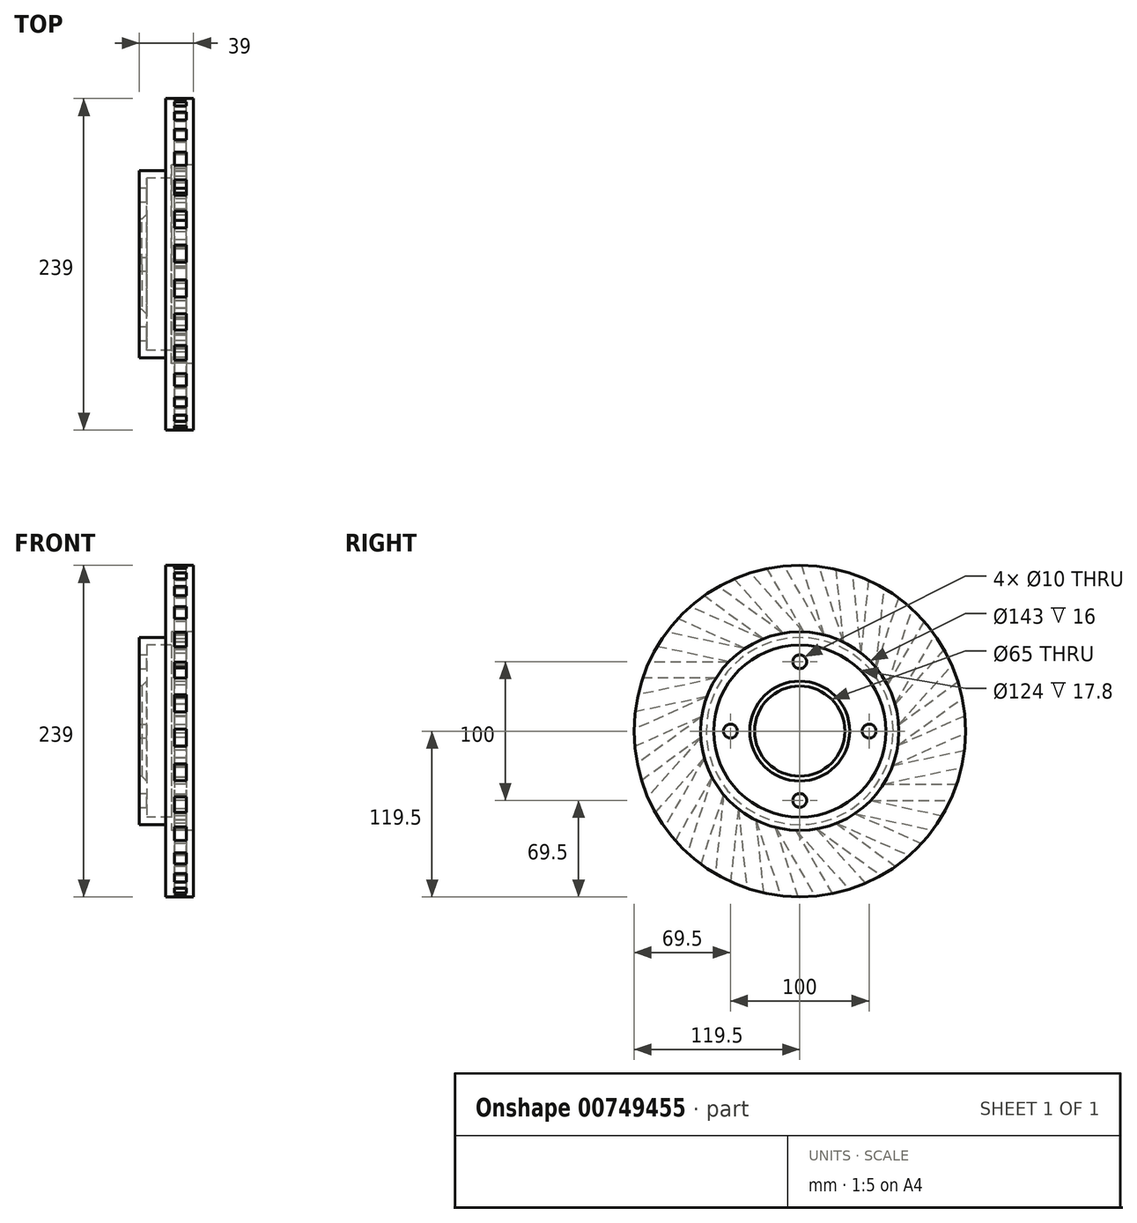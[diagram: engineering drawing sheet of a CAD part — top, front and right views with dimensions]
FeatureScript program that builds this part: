
annotation { "Feature Type Name" : "Feature", "Feature Type Description" : "" }
export const myFeature = defineFeature(function(context is Context, id is Id, definition is map)
    precondition{}
    {
        {
            var Q0;
            Q0=qCreatedBy(makeId("Front.planeOp"),FACE);
            var sketch = newSketch(context, id + "F0", { "sketchPlane" : qUnion([Q0])});
            skLineSegment(sketch, "E0", {"start": v(0, 32.5) * mm, "end": v(0, 67.4) * mm});
            skLineSegment(sketch, "E1", {"start": v(0, 67.4) * mm, "end": v(19, 67.4) * mm});
            skLineSegment(sketch, "E2", {"start": v(19, 67.4) * mm, "end": v(19, 119.5) * mm});
            skLineSegment(sketch, "E3", {"start": v(19, 119.5) * mm, "end": v(39, 119.5) * mm});
            skLineSegment(sketch, "E4", {"start": v(39, 119.5) * mm, "end": v(39, 71.5) * mm});
            skLineSegment(sketch, "E5", {"start": v(39, 71.5) * mm, "end": v(23, 71.5) * mm});
            skLineSegment(sketch, "E6", {"start": v(23, 71.5) * mm, "end": v(23, 62) * mm});
            skLineSegment(sketch, "E7", {"start": v(23, 62) * mm, "end": v(5.2, 62) * mm});
            skLineSegment(sketch, "E8", {"start": v(5.2, 62) * mm, "end": v(5.2, 32.5) * mm});
            skLineSegment(sketch, "E9", {"start": v(5.2, 32.5) * mm, "end": v(0, 32.5) * mm});
            skLineSegment(sketch, "E10", {"start": v(2.46, 0) * mm, "end": v(32.27, 0) * mm, "construction": true});
            skSolve(sketch);
        }
        {
            var Q0;
            Q0=makeQuery(id+"F0.imprint","IMPRINT",FACE,{"disambiguationData":[TD([[makeQuery(id+"F0.imprint","IMPRINT",EDGE,{"derivedFrom":sQuery(id+"F0.wireOp",EDGE,"E0")}),-1.0]])]});
            var Q1;
            Q1=sQuery(id+"F0.wireOp",EDGE,"E5");
            var Q2;
            Q2=sQuery(id+"F0.wireOp",EDGE,"E4");
            var Q3;
            Q3=sQuery(id+"F0.wireOp",EDGE,"E8");
            var Q4;
            Q4=sQuery(id+"F0.wireOp",EDGE,"E3");
            var Q5;
            Q5=sQuery(id+"F0.wireOp",EDGE,"E7");
            var Q6;
            Q6=sQuery(id+"F0.wireOp",EDGE,"E2");
            var Q7;
            Q7=sQuery(id+"F0.wireOp",EDGE,"E1");
            var Q8;
            Q8=sQuery(id+"F0.wireOp",EDGE,"E0");
            var Q9;
            Q9=sQuery(id+"F0.wireOp",EDGE,"E9");
            var Q10;
            Q10=sQuery(id+"F0.wireOp",EDGE,"E6");
            var Q11;
            Q11=sQuery(id+"F0.wireOp",EDGE,"E10");
            revolve(context, id + "F1", {"surfaceOperationType" : NewSurfaceOperationType.NEW, "entities" : qUnion([Q0]), "surfaceEntities" : qUnion([Q1, Q2, Q3, Q4, Q5, Q6, Q7, Q8, Q9, Q10]), "axis" : qUnion([Q11]), "revolveType" : RevolveType.FULL});
        }
        {
            var Q0;
            Q0=makeQuery(id+"F1.opRevolve","SWEPT_EDGE",EDGE,{"disambiguationData":[OSD([sQuery(id+"F0.wireOp",VERTEX,"E9.start")])]});
            var Q1;
            Q1=makeQuery(id+"F1.opRevolve","SWEPT_EDGE",EDGE,{"disambiguationData":[OSD([sQuery(id+"F0.wireOp",EDGE,"E8"),sQuery(id+"F0.wireOp",EDGE,"E9")])]});
            chamfer(context, id + "F2", {"entities" : qUnion([Q0, Q1]), "width" : 3.5 * mm, "tangentPropagation" : true});
        }
        {
            var Q0;
            Q0=makeQuery(id+"F1.opRevolve","SWEPT_FACE",FACE,{"disambiguationData":[OSD([sQuery(id+"F0.wireOp",EDGE,"E2")])]});
            var sketch = newSketch(context, id + "F3", { "sketchPlane" : qUnion([Q0])});
            skCircle(sketch, "E11", {"center": v(0, 50) * mm, "radius": 5 * mm});
            skCircle(sketch, "E12.1.0", {"center": v(-50, 0) * mm, "radius": 5 * mm});
            skCircle(sketch, "E12.2.0", {"center": v(0, -50) * mm, "radius": 5 * mm});
            skCircle(sketch, "E12.3.0", {"center": v(50, 0) * mm, "radius": 5 * mm});
            skPoint(sketch, "E12.center", {"position": v(0, 0) * mm});
            skSolve(sketch);
        }
        {
            var Q0;
            Q0=makeQuery(id+"F3.imprint","IMPRINT",FACE,{"disambiguationData":[TD([[makeQuery(id+"F3.imprint","IMPRINT",EDGE,{"derivedFrom":sQuery(id+"F3.wireOp",EDGE,"E11")}),1.0]])]});
            var Q1;
            Q1=makeQuery(id+"F3.imprint","IMPRINT",FACE,{"disambiguationData":[TD([[makeQuery(id+"F3.imprint","IMPRINT",EDGE,{"derivedFrom":sQuery(id+"F3.wireOp",EDGE,"E12.1.0")}),1.0]])]});
            var Q2;
            Q2=makeQuery(id+"F3.imprint","IMPRINT",FACE,{"disambiguationData":[TD([[makeQuery(id+"F3.imprint","IMPRINT",EDGE,{"derivedFrom":sQuery(id+"F3.wireOp",EDGE,"E12.3.0")}),1.0]])]});
            var Q3;
            Q3=makeQuery(id+"F3.imprint","IMPRINT",FACE,{"disambiguationData":[TD([[makeQuery(id+"F3.imprint","IMPRINT",EDGE,{"derivedFrom":sQuery(id+"F3.wireOp",EDGE,"E12.2.0")}),1.0]])]});
            extrude(context, id + "F4", {"entities" : qUnion([Q0, Q1, Q2, Q3]), "operationType" : NewBodyOperationType.REMOVE, "endBound" : BoundingType.THROUGH_ALL, "depth" : 25 * mm, "offsetDistance" : 25 * mm});
        }
        {
            var Q0;
            Q0=makeQuery(id+"F1.opRevolve","SWEPT_FACE",FACE,{"disambiguationData":[OSD([sQuery(id+"F0.wireOp",EDGE,"E4")])]});
            var sketch = newSketch(context, id + "F5", { "sketchPlane" : qUnion([Q0])});
            skLineSegment(sketch, "E13.bottom", {"start": v(-37.23, 38.26) * mm, "end": v(-217.01, 38.26) * mm});
            skLineSegment(sketch, "E13.top", {"start": v(-37.23, 49.86) * mm, "end": v(-217.01, 49.86) * mm});
            skLineSegment(sketch, "E13.left", {"start": v(-37.23, 38.26) * mm, "end": v(-37.23, 49.86) * mm});
            skLineSegment(sketch, "E13.right", {"start": v(-217.01, 38.26) * mm, "end": v(-217.01, 49.86) * mm});
            skPoint(sketch, "E13.middle", {"position": v(-127.12, 44.06) * mm});
            skLineSegment(sketch, "E14.1.0", {"start": v(-46.78, 41.03) * mm, "end": v(-222.63, 3.65) * mm});
            skLineSegment(sketch, "E14.1.1", {"start": v(-44.37, 29.68) * mm, "end": v(-46.78, 41.03) * mm});
            skLineSegment(sketch, "E14.1.2", {"start": v(-44.37, 29.68) * mm, "end": v(-220.22, -7.7) * mm});
            skLineSegment(sketch, "E14.1.3", {"start": v(-220.22, -7.7) * mm, "end": v(-222.63, 3.65) * mm});
            skLineSegment(sketch, "E14.2.0", {"start": v(-54.29, 30.4) * mm, "end": v(-218.53, -42.72) * mm});
            skLineSegment(sketch, "E14.2.1", {"start": v(-49.57, 19.81) * mm, "end": v(-54.29, 30.4) * mm});
            skLineSegment(sketch, "E14.2.2", {"start": v(-49.57, 19.81) * mm, "end": v(-213.81, -53.31) * mm});
            skLineSegment(sketch, "E14.2.3", {"start": v(-213.81, -53.31) * mm, "end": v(-218.53, -42.72) * mm});
            skLineSegment(sketch, "E14.3.0", {"start": v(-59.42, 18.46) * mm, "end": v(-204.87, -87.22) * mm});
            skLineSegment(sketch, "E14.3.1", {"start": v(-52.6, 9.07) * mm, "end": v(-59.42, 18.46) * mm});
            skLineSegment(sketch, "E14.3.2", {"start": v(-52.6, 9.07) * mm, "end": v(-198.05, -96.6) * mm});
            skLineSegment(sketch, "E14.3.3", {"start": v(-198.05, -96.6) * mm, "end": v(-204.87, -87.22) * mm});
            skLineSegment(sketch, "E14.4.0", {"start": v(-61.96, 5.7) * mm, "end": v(-182.26, -127.9) * mm});
            skLineSegment(sketch, "E14.4.1", {"start": v(-53.34, -2.06) * mm, "end": v(-61.96, 5.7) * mm});
            skLineSegment(sketch, "E14.4.2", {"start": v(-53.34, -2.06) * mm, "end": v(-173.64, -135.67) * mm});
            skLineSegment(sketch, "E14.4.3", {"start": v(-173.64, -135.67) * mm, "end": v(-182.26, -127.9) * mm});
            skLineSegment(sketch, "E14.5.0", {"start": v(-61.8, -7.3) * mm, "end": v(-151.68, -163) * mm});
            skLineSegment(sketch, "E14.5.1", {"start": v(-51.75, -13.1) * mm, "end": v(-61.8, -7.3) * mm});
            skLineSegment(sketch, "E14.5.2", {"start": v(-51.75, -13.1) * mm, "end": v(-141.64, -168.8) * mm});
            skLineSegment(sketch, "E14.5.3", {"start": v(-141.64, -168.8) * mm, "end": v(-151.68, -163) * mm});
            skLineSegment(sketch, "E14.6.0", {"start": v(-58.92, -20) * mm, "end": v(-114.48, -190.98) * mm});
            skLineSegment(sketch, "E14.6.1", {"start": v(-47.89, -23.58) * mm, "end": v(-58.92, -20) * mm});
            skLineSegment(sketch, "E14.6.2", {"start": v(-47.89, -23.58) * mm, "end": v(-103.45, -194.57) * mm});
            skLineSegment(sketch, "E14.6.3", {"start": v(-103.45, -194.57) * mm, "end": v(-114.48, -190.98) * mm});
            skLineSegment(sketch, "E14.7.0", {"start": v(-53.48, -31.8) * mm, "end": v(-72.27, -210.6) * mm});
            skLineSegment(sketch, "E14.7.1", {"start": v(-41.94, -33.02) * mm, "end": v(-53.48, -31.8) * mm});
            skLineSegment(sketch, "E14.7.2", {"start": v(-41.94, -33.02) * mm, "end": v(-60.73, -211.82) * mm});
            skLineSegment(sketch, "E14.7.3", {"start": v(-60.73, -211.82) * mm, "end": v(-72.27, -210.6) * mm});
            skLineSegment(sketch, "E14.8.0", {"start": v(-45.7, -42.23) * mm, "end": v(-26.9, -221.03) * mm});
            skLineSegment(sketch, "E14.8.1", {"start": v(-34.16, -41.02) * mm, "end": v(-45.7, -42.23) * mm});
            skLineSegment(sketch, "E14.8.2", {"start": v(-34.16, -41.02) * mm, "end": v(-15.37, -219.82) * mm});
            skLineSegment(sketch, "E14.8.3", {"start": v(-15.37, -219.82) * mm, "end": v(-26.9, -221.03) * mm});
            skLineSegment(sketch, "E14.9.0", {"start": v(-35.91, -50.81) * mm, "end": v(19.64, -221.8) * mm});
            skLineSegment(sketch, "E14.9.1", {"start": v(-24.88, -47.23) * mm, "end": v(-35.91, -50.81) * mm});
            skLineSegment(sketch, "E14.9.2", {"start": v(-24.88, -47.23) * mm, "end": v(30.67, -218.21) * mm});
            skLineSegment(sketch, "E14.9.3", {"start": v(30.67, -218.21) * mm, "end": v(19.64, -221.8) * mm});
            skLineSegment(sketch, "E14.10.0", {"start": v(-24.57, -57.17) * mm, "end": v(65.33, -212.87) * mm});
            skLineSegment(sketch, "E14.10.1", {"start": v(-14.52, -51.37) * mm, "end": v(-24.57, -57.17) * mm});
            skLineSegment(sketch, "E14.10.2", {"start": v(-14.52, -51.37) * mm, "end": v(75.37, -207.07) * mm});
            skLineSegment(sketch, "E14.10.3", {"start": v(75.37, -207.07) * mm, "end": v(65.33, -212.87) * mm});
            skLineSegment(sketch, "E14.11.0", {"start": v(-12.14, -61.03) * mm, "end": v(108.16, -194.63) * mm});
            skLineSegment(sketch, "E14.11.1", {"start": v(-3.52, -53.26) * mm, "end": v(-12.14, -61.03) * mm});
            skLineSegment(sketch, "E14.11.2", {"start": v(-3.52, -53.26) * mm, "end": v(116.78, -186.87) * mm});
            skLineSegment(sketch, "E14.11.3", {"start": v(116.78, -186.87) * mm, "end": v(108.16, -194.63) * mm});
            skLineSegment(sketch, "E14.12.0", {"start": v(0.8, -62.22) * mm, "end": v(146.26, -167.9) * mm});
            skLineSegment(sketch, "E14.12.1", {"start": v(7.63, -52.83) * mm, "end": v(0.8, -62.22) * mm});
            skLineSegment(sketch, "E14.12.2", {"start": v(7.63, -52.83) * mm, "end": v(153.08, -158.5) * mm});
            skLineSegment(sketch, "E14.12.3", {"start": v(153.08, -158.5) * mm, "end": v(146.26, -167.9) * mm});
            skLineSegment(sketch, "E14.13.0", {"start": v(13.73, -60.69) * mm, "end": v(177.97, -133.81) * mm});
            skLineSegment(sketch, "E14.13.1", {"start": v(18.45, -50.1) * mm, "end": v(13.73, -60.69) * mm});
            skLineSegment(sketch, "E14.13.2", {"start": v(18.45, -50.1) * mm, "end": v(182.69, -123.22) * mm});
            skLineSegment(sketch, "E14.13.3", {"start": v(182.69, -123.22) * mm, "end": v(177.97, -133.81) * mm});
            skLineSegment(sketch, "E14.14.0", {"start": v(26.05, -56.5) * mm, "end": v(201.9, -93.89) * mm});
            skLineSegment(sketch, "E14.14.1", {"start": v(28.46, -45.16) * mm, "end": v(26.05, -56.5) * mm});
            skLineSegment(sketch, "E14.14.2", {"start": v(28.46, -45.16) * mm, "end": v(204.31, -82.54) * mm});
            skLineSegment(sketch, "E14.14.3", {"start": v(204.31, -82.54) * mm, "end": v(201.9, -93.89) * mm});
            skLineSegment(sketch, "E14.15.0", {"start": v(37.23, -49.86) * mm, "end": v(217.01, -49.86) * mm});
            skLineSegment(sketch, "E14.15.1", {"start": v(37.23, -38.26) * mm, "end": v(37.23, -49.86) * mm});
            skLineSegment(sketch, "E14.15.2", {"start": v(37.23, -38.26) * mm, "end": v(217.01, -38.26) * mm});
            skLineSegment(sketch, "E14.15.3", {"start": v(217.01, -38.26) * mm, "end": v(217.01, -49.86) * mm});
            skLineSegment(sketch, "E14.16.0", {"start": v(46.78, -41.03) * mm, "end": v(222.63, -3.65) * mm});
            skLineSegment(sketch, "E14.16.1", {"start": v(44.37, -29.68) * mm, "end": v(46.78, -41.03) * mm});
            skLineSegment(sketch, "E14.16.2", {"start": v(44.37, -29.68) * mm, "end": v(220.22, 7.7) * mm});
            skLineSegment(sketch, "E14.16.3", {"start": v(220.22, 7.7) * mm, "end": v(222.63, -3.65) * mm});
            skLineSegment(sketch, "E14.17.0", {"start": v(54.29, -30.4) * mm, "end": v(218.53, 42.72) * mm});
            skLineSegment(sketch, "E14.17.1", {"start": v(49.57, -19.81) * mm, "end": v(54.29, -30.4) * mm});
            skLineSegment(sketch, "E14.17.2", {"start": v(49.57, -19.81) * mm, "end": v(213.81, 53.31) * mm});
            skLineSegment(sketch, "E14.17.3", {"start": v(213.81, 53.31) * mm, "end": v(218.53, 42.72) * mm});
            skLineSegment(sketch, "E14.18.0", {"start": v(59.42, -18.46) * mm, "end": v(204.87, 87.22) * mm});
            skLineSegment(sketch, "E14.18.1", {"start": v(52.6, -9.07) * mm, "end": v(59.42, -18.46) * mm});
            skLineSegment(sketch, "E14.18.2", {"start": v(52.6, -9.07) * mm, "end": v(198.05, 96.6) * mm});
            skLineSegment(sketch, "E14.18.3", {"start": v(198.05, 96.6) * mm, "end": v(204.87, 87.22) * mm});
            skLineSegment(sketch, "E14.19.0", {"start": v(61.96, -5.7) * mm, "end": v(182.26, 127.9) * mm});
            skLineSegment(sketch, "E14.19.1", {"start": v(53.34, 2.06) * mm, "end": v(61.96, -5.7) * mm});
            skLineSegment(sketch, "E14.19.2", {"start": v(53.34, 2.06) * mm, "end": v(173.64, 135.67) * mm});
            skLineSegment(sketch, "E14.19.3", {"start": v(173.64, 135.67) * mm, "end": v(182.26, 127.9) * mm});
            skLineSegment(sketch, "E14.20.0", {"start": v(61.8, 7.3) * mm, "end": v(151.68, 163) * mm});
            skLineSegment(sketch, "E14.20.1", {"start": v(51.75, 13.1) * mm, "end": v(61.8, 7.3) * mm});
            skLineSegment(sketch, "E14.20.2", {"start": v(51.75, 13.1) * mm, "end": v(141.64, 168.8) * mm});
            skLineSegment(sketch, "E14.20.3", {"start": v(141.64, 168.8) * mm, "end": v(151.68, 163) * mm});
            skLineSegment(sketch, "E14.21.0", {"start": v(58.92, 20) * mm, "end": v(114.48, 190.98) * mm});
            skLineSegment(sketch, "E14.21.1", {"start": v(47.89, 23.58) * mm, "end": v(58.92, 20) * mm});
            skLineSegment(sketch, "E14.21.2", {"start": v(47.89, 23.58) * mm, "end": v(103.45, 194.57) * mm});
            skLineSegment(sketch, "E14.21.3", {"start": v(103.45, 194.57) * mm, "end": v(114.48, 190.98) * mm});
            skLineSegment(sketch, "E14.22.0", {"start": v(53.48, 31.8) * mm, "end": v(72.27, 210.6) * mm});
            skLineSegment(sketch, "E14.22.1", {"start": v(41.94, 33.02) * mm, "end": v(53.48, 31.8) * mm});
            skLineSegment(sketch, "E14.22.2", {"start": v(41.94, 33.02) * mm, "end": v(60.73, 211.82) * mm});
            skLineSegment(sketch, "E14.22.3", {"start": v(60.73, 211.82) * mm, "end": v(72.27, 210.6) * mm});
            skLineSegment(sketch, "E14.23.0", {"start": v(45.7, 42.23) * mm, "end": v(26.9, 221.03) * mm});
            skLineSegment(sketch, "E14.23.1", {"start": v(34.16, 41.02) * mm, "end": v(45.7, 42.23) * mm});
            skLineSegment(sketch, "E14.23.2", {"start": v(34.16, 41.02) * mm, "end": v(15.37, 219.82) * mm});
            skLineSegment(sketch, "E14.23.3", {"start": v(15.37, 219.82) * mm, "end": v(26.9, 221.03) * mm});
            skLineSegment(sketch, "E14.24.0", {"start": v(35.91, 50.81) * mm, "end": v(-19.64, 221.8) * mm});
            skLineSegment(sketch, "E14.24.1", {"start": v(24.88, 47.23) * mm, "end": v(35.91, 50.81) * mm});
            skLineSegment(sketch, "E14.24.2", {"start": v(24.88, 47.23) * mm, "end": v(-30.67, 218.21) * mm});
            skLineSegment(sketch, "E14.24.3", {"start": v(-30.67, 218.21) * mm, "end": v(-19.64, 221.8) * mm});
            skLineSegment(sketch, "E14.25.0", {"start": v(24.57, 57.17) * mm, "end": v(-65.33, 212.87) * mm});
            skLineSegment(sketch, "E14.25.1", {"start": v(14.52, 51.37) * mm, "end": v(24.57, 57.17) * mm});
            skLineSegment(sketch, "E14.25.2", {"start": v(14.52, 51.37) * mm, "end": v(-75.37, 207.07) * mm});
            skLineSegment(sketch, "E14.25.3", {"start": v(-75.37, 207.07) * mm, "end": v(-65.33, 212.87) * mm});
            skLineSegment(sketch, "E14.26.0", {"start": v(12.14, 61.03) * mm, "end": v(-108.16, 194.63) * mm});
            skLineSegment(sketch, "E14.26.1", {"start": v(3.52, 53.26) * mm, "end": v(12.14, 61.03) * mm});
            skLineSegment(sketch, "E14.26.2", {"start": v(3.52, 53.26) * mm, "end": v(-116.78, 186.87) * mm});
            skLineSegment(sketch, "E14.26.3", {"start": v(-116.78, 186.87) * mm, "end": v(-108.16, 194.63) * mm});
            skLineSegment(sketch, "E14.27.0", {"start": v(-0.8, 62.22) * mm, "end": v(-146.26, 167.9) * mm});
            skLineSegment(sketch, "E14.27.1", {"start": v(-7.63, 52.83) * mm, "end": v(-0.8, 62.22) * mm});
            skLineSegment(sketch, "E14.27.2", {"start": v(-7.63, 52.83) * mm, "end": v(-153.08, 158.5) * mm});
            skLineSegment(sketch, "E14.27.3", {"start": v(-153.08, 158.5) * mm, "end": v(-146.26, 167.9) * mm});
            skLineSegment(sketch, "E14.28.0", {"start": v(-13.73, 60.69) * mm, "end": v(-177.97, 133.81) * mm});
            skLineSegment(sketch, "E14.28.1", {"start": v(-18.45, 50.1) * mm, "end": v(-13.73, 60.69) * mm});
            skLineSegment(sketch, "E14.28.2", {"start": v(-18.45, 50.1) * mm, "end": v(-182.69, 123.22) * mm});
            skLineSegment(sketch, "E14.28.3", {"start": v(-182.69, 123.22) * mm, "end": v(-177.97, 133.81) * mm});
            skLineSegment(sketch, "E14.29.0", {"start": v(-26.05, 56.5) * mm, "end": v(-201.9, 93.89) * mm});
            skLineSegment(sketch, "E14.29.1", {"start": v(-28.46, 45.16) * mm, "end": v(-26.05, 56.5) * mm});
            skLineSegment(sketch, "E14.29.2", {"start": v(-28.46, 45.16) * mm, "end": v(-204.31, 82.54) * mm});
            skLineSegment(sketch, "E14.29.3", {"start": v(-204.31, 82.54) * mm, "end": v(-201.9, 93.89) * mm});
            skPoint(sketch, "E14.center", {"position": v(0, 0) * mm});
            skSolve(sketch);
        }
        {
            var Q0;
            Q0 = qSketchRegion(id + "F5", true);
            extrude(context, id + "F6", {"entities" : qUnion([Q0]), "operationType" : NewBodyOperationType.REMOVE, "oppositeDirection" : true, "depth" : 13.6 * mm, "offsetDistance" : 25 * mm, "hasSecondDirection" : true, "secondDirectionOppositeDirection" : true, "secondDirectionDepth" : 5.3 * mm});
        }
    });
